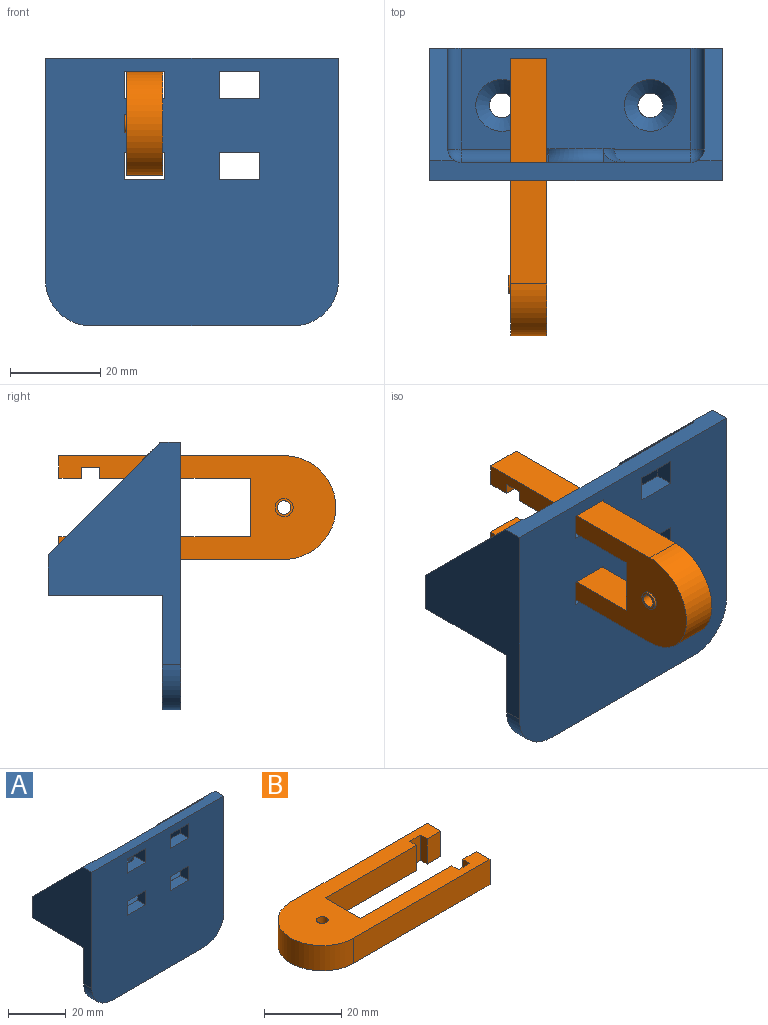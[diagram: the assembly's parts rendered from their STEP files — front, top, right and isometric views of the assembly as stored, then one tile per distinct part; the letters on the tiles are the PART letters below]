
ASSEMBLY  parts=2 mates=1
PART A: 49 faces, bbox 65x29.4x59.4 mm
  f0: plane 51x27mm, normal (0,1,0), area 767.2mm2, adj f12,f15,f16,f17,f18,f19,f20,f21
  f1: plane 65x59.4mm, normal (0,-1,0), area 3602.1mm2, adj f3,f4,f5,f12,f15,f16,f17,f18
  f2: plane 12x2.21mm, normal (0,1,0), area 12.7mm2, adj f24,f30,f32,f40
  f3: plane 49.4x29.4mm, normal (-1,0,0), area 748.7mm2, adj f1,f7,f8,f9,f12,f13,f45
  f4: plane 45x4mm, normal (0,0,-1), area 180mm2, adj f1,f7,f45,f46
  f5: plane 49.4x29.4mm, normal (1,0,0), area 748.7mm2, adj f1,f7,f8,f9,f12,f14,f46
  f6: plane 51x22.4mm, normal (0,0,1), area 934.7mm2, adj f9,f36,f39,f40,f47,f48
  f7: plane 65x25.4mm, normal (0,1,0), area 1608.1mm2, adj f3,f4,f5,f8,f45,f46
  f8: plane 65x25.4mm, normal (0,0,-1), area 1603.5mm2, adj f3,f5,f7,f9,f43,f44
  f9: plane 65x9mm, normal (0,1,0), area 303.9mm2, adj f3,f5,f6,f8,f10,f11,f13,f14
  f10: plane 24.4x22.4mm, normal (-1,0,0), area 295.7mm2, adj f9,f14,f36,f37
  f11: plane 24.4x22.4mm, normal (1,0,0), area 295.7mm2, adj f9,f13,f39,f42
  f12: plane 65x4.4mm, normal (0,0,1), area 264.8mm2, adj f0,f1,f3,f5,f13,f14,f37,f42
  f13: plane 25x25mm, normal (0,0.71,0.71), area 143mm2, adj f3,f9,f11,f12,f42
  f14: plane 25x25mm, normal (0,0.71,0.71), area 143mm2, adj f5,f9,f10,f12,f37
  f15: plane 9x4mm, normal (0,0,-1), area 36mm2, adj f0,f1,f16,f18
  f16: plane 6x4mm, normal (-1,0,0), area 24mm2, adj f0,f1,f15,f17
  f17: plane 9x7mm, normal (0,0,1), area 38.6mm2, adj f0,f1,f16,f18,f34
  f18: plane 7x6mm, normal (1,0,0), area 26.6mm2, adj f0,f1,f15,f17,f35
  f19: plane 9x4mm, normal (0,0,-1), area 36mm2, adj f0,f1,f20,f22
  f20: plane 7x6mm, normal (-1,0,0), area 26.6mm2, adj f0,f1,f19,f21,f35
  f21: plane 9x7mm, normal (0,0,1), area 38.6mm2, adj f0,f1,f20,f22,f33
  f22: plane 6x4mm, normal (1,0,0), area 24mm2, adj f0,f1,f19,f21
  f23: plane 9x7mm, normal (0,0,-1), area 38.6mm2, adj f0,f1,f24,f26,f33
  f24: plane 7x6mm, normal (-1,0,0), area 26.6mm2, adj f1,f2,f23,f25,f32
  f25: plane 9x4mm, normal (0,0,1), area 36mm2, adj f1,f24,f26,f40
  f26: plane 6x4mm, normal (1,0,0), area 24mm2, adj f0,f1,f23,f25
  f27: plane 9x7mm, normal (0,0,-1), area 38.6mm2, adj f0,f1,f28,f30,f34
  f28: plane 6x4mm, normal (-1,0,0), area 24mm2, adj f0,f1,f27,f29
  f29: plane 9x4mm, normal (0,0,1), area 36mm2, adj f1,f28,f30,f40
  f30: plane 7x6mm, normal (1,0,0), area 26.6mm2, adj f1,f2,f27,f29,f32
  f31: plane 16.97x16.97mm, normal (0,1,0), area 226.2mm2, adj f32,f33,f34,f35
  f32: torus R=11.49mm, axis (0,-1,0), area 61.3mm2, adj f2,f24,f30,f31
  f33: torus R=11.49mm, axis (0,-1,0), area 61.3mm2, adj f0,f21,f23,f31
  f34: torus R=11.49mm, axis (0,-1,0), area 61.3mm2, adj f0,f17,f27,f31
  f35: torus R=11.49mm, axis (0,-1,0), area 61.3mm2, adj f0,f18,f20,f31
  f36: cylinder r=3mm len=22.4mm, axis (0,-1,0), area 105.6mm2, adj f6,f9,f10,f38
  f37: cylinder r=3mm len=27mm, axis (0,0,-1), area 123.6mm2, adj f0,f10,f12,f14,f38
  f38: sphere r=3mm, area 14.1mm2, adj f36,f37,f40
  f39: cylinder r=3mm len=22.4mm, axis (0,1,0), area 105.6mm2, adj f6,f9,f11,f41
  f40: cylinder r=3mm len=51mm, axis (-1,0,0), area 240.3mm2, adj f0,f2,f6,f25,f29,f38,f41
  f41: sphere r=3mm, area 14.1mm2, adj f39,f40,f42
  f42: cylinder r=3mm len=27mm, axis (0,0,1), area 123.6mm2, adj f0,f11,f12,f13,f41
  f43: cylinder r=2.75mm len=5.5mm, axis (0,0,1), area 17.3mm2, adj f8,f48
  f44: cylinder r=2.75mm len=5.5mm, axis (0,0,1), area 17.3mm2, adj f8,f47
  f45: cylinder r=10mm len=10mm, axis (0,-1,0), area 62.8mm2, adj f1,f3,f4,f7
  f46: cylinder r=10mm len=10mm, axis (0,1,0), area 62.8mm2, adj f1,f4,f5,f7
  f47: cone r=2.75mm half-angle=45deg, axis (0,0,1), area 113.3mm2, adj f6,f44
  f48: cone r=2.75mm half-angle=45deg, axis (0,0,1), area 113.3mm2, adj f6,f43
PART B: 21 faces, bbox 61.5x23x8.5 mm
  f0: plane 50x8mm, normal (0,1,0), area 400mm2, adj f1,f15,f17,f18
  f1: cylinder r=11.5mm len=23mm, axis (0,0,-1), area 289mm2, adj f0,f2,f17,f18
  f2: plane 50x8mm, normal (0,-1,0), area 400mm2, adj f1,f3,f17,f18
  f3: plane 8x5mm, normal (1,0,0), area 40mm2, adj f2,f4,f17,f18
  f4: plane 8x5mm, normal (0,1,0), area 40mm2, adj f3,f5,f17,f18
  f5: plane 8x2.5mm, normal (-1,0,0), area 20mm2, adj f4,f6,f17,f18
  f6: plane 8x4mm, normal (0,1,0), area 32mm2, adj f5,f7,f17,f18
  f7: plane 8x2.5mm, normal (1,0,0), area 20mm2, adj f6,f8,f17,f18
  f8: plane 33.5x8mm, normal (0,1,0), area 268mm2, adj f7,f9,f17,f18
  f9: plane 13x8mm, normal (1,0,0), area 104mm2, adj f8,f10,f17,f18
  f10: plane 33.5x8mm, normal (0,-1,0), area 268mm2, adj f9,f11,f17,f18
  f11: plane 8x2.5mm, normal (1,0,0), area 20mm2, adj f10,f12,f17,f18
  f12: plane 8x4mm, normal (0,-1,0), area 32mm2, adj f11,f13,f17,f18
  f13: plane 8x2.5mm, normal (-1,0,0), area 20mm2, adj f12,f14,f17,f18
  f14: plane 8x5mm, normal (0,-1,0), area 40mm2, adj f13,f15,f17,f18
  f15: plane 8x5mm, normal (1,0,0), area 40mm2, adj f0,f14,f17,f18
  f16: cylinder r=1.5mm len=8.5mm, axis (0,0,-1), area 80.1mm2, adj f17,f20
  f17: plane 61.5x23mm, normal (0,0,1), area 778.2mm2, adj f0,f1,f2,f3,f4,f5,f6,f7
  f18: plane 61.5x23mm, normal (0,0,-1), area 772.7mm2, adj f0,f1,f2,f3,f4,f5,f6,f7
  f19: cylinder r=2mm len=4mm, axis (0,0,1), area 6.3mm2, adj f18,f20
  f20: plane 4x4mm, normal (0,0,-1), area 5.5mm2, adj f16,f19
PLACE A t=(-65.39,-19.09,28.55)mm
PLACE B rot(axis=(0.58,0.58,0.58),120deg) t=(-79.89,-21.09,67.75)mm
MATE fastened B.f0 <-> A.f19  axis (0,0,1) through (-75.89,-21.09,70.25)mm
